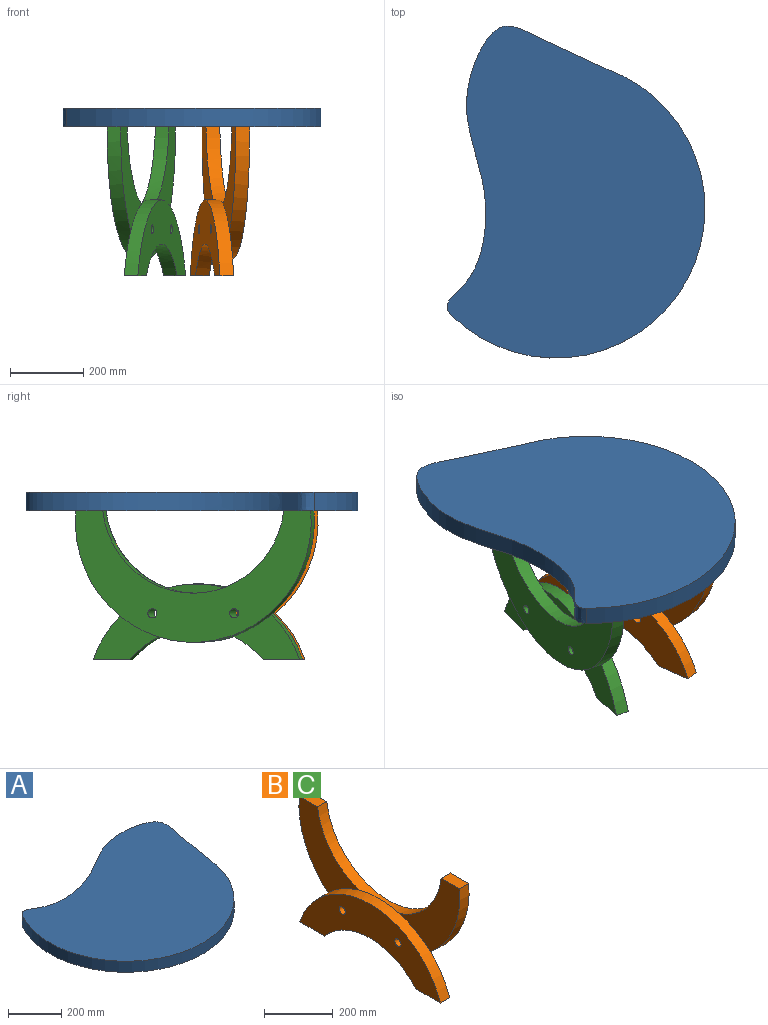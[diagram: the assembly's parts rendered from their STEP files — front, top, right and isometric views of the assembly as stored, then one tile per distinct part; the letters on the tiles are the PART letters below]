
ASSEMBLY  parts=3 mates=2
PART A: 4 faces, bbox 872.4x740.9x50.8 mm
  f0: extruded ~802.2x351.8mm, area 59062mm2, adj f1,f2,f3
  f1: cylinder r=406.4mm len=811.48mm, axis (0,0,-1), area 74006.5mm2, adj f0,f2,f3
  f2: plane 872.36x740.91mm, normal (0,0,1), area 455862.2mm2, adj f0,f1
  f3: plane 872.36x740.91mm, normal (0,0,-1), area 455862.2mm2, adj f0,f1
PART B: 18 faces, bbox 76.2x660.4x406.4 mm
  f0: plane 283.23x247.01mm, normal (-1,0,0), area 30056.5mm2, adj f2,f4,f6,f12
  f1: plane 204.47x38.45mm, normal (-1,0,0), area 5280.3mm2, adj f4,f14
  f2: cylinder r=255.43mm len=507.17mm, axis (-1,0,0), area 28231.1mm2, adj f0,f3,f6,f8,f9,f17
  f3: plane 75.39x38.1mm, normal (0,0,1), area 2872.2mm2, adj f2,f4,f8,f9
  f4: cylinder r=330.2mm len=660.4mm, axis (-1,0,0), area 41696.5mm2, adj f0,f1,f3,f6,f8,f9,f10,f11
  f5: cylinder r=12.7mm len=76.2mm, axis (-1,0,0), area 6080.5mm2, adj f8,f16
  f6: plane 75.39x38.1mm, normal (0,0,1), area 2872.2mm2, adj f0,f2,f4,f8
  f7: cylinder r=12.7mm len=76.2mm, axis (-1,0,0), area 6080.5mm2, adj f8,f16
  f8: plane 660.4x358.69mm, normal (1,0,0), area 102185.5mm2, adj f2,f3,f4,f5,f6,f7
  f9: plane 283.23x247.01mm, normal (-1,0,0), area 30056.5mm2, adj f2,f3,f4,f12
  f10: plane 186.5x123.17mm, normal (1,0,0), area 12200.4mm2, adj f4,f12,f13,f14
  f11: plane 186.5x123.17mm, normal (1,0,0), area 12200.4mm2, adj f4,f12,f14,f15
  f12: cylinder r=304.8mm len=577.46mm, axis (1,0,0), area 28907.5mm2, adj f0,f9,f10,f11,f13,f15,f16,f17
  f13: plane 101.6x38.1mm, normal (0,0,-1), area 3871mm2, adj f10,f12,f14,f16
  f14: cylinder r=246.29mm len=374.26mm, axis (1,0,0), area 16196.2mm2, adj f1,f10,f11,f13,f15,f16
  f15: plane 101.6x38.1mm, normal (0,0,-1), area 3871mm2, adj f11,f12,f14,f16
  f16: plane 577.46x207.14mm, normal (-1,0,0), area 64035.1mm2, adj f5,f7,f12,f13,f14,f15
  f17: plane 166.38x25.5mm, normal (1,0,0), area 2841.9mm2, adj f2,f12
PART C: same geometry as B
PLACE A rot(axis=(0,0,1),75deg) t=(74.16,-480.68,-487.22)mm
PLACE B rot(axis=(0,0,1),8deg) t=(202.18,-450.91,-456.54)mm
PLACE C rot(axis=(0,0,1),167deg) t=(9.06,-446.05,-456.54)mm
MATE planar B.f3 <-> A.f3  axis (0,0,1) through (242.72,-739.35,-487.22)mm
MATE planar A.f3 <-> C.f6  axis (0,0,-1) through (124.07,-462.58,-487.22)mm
